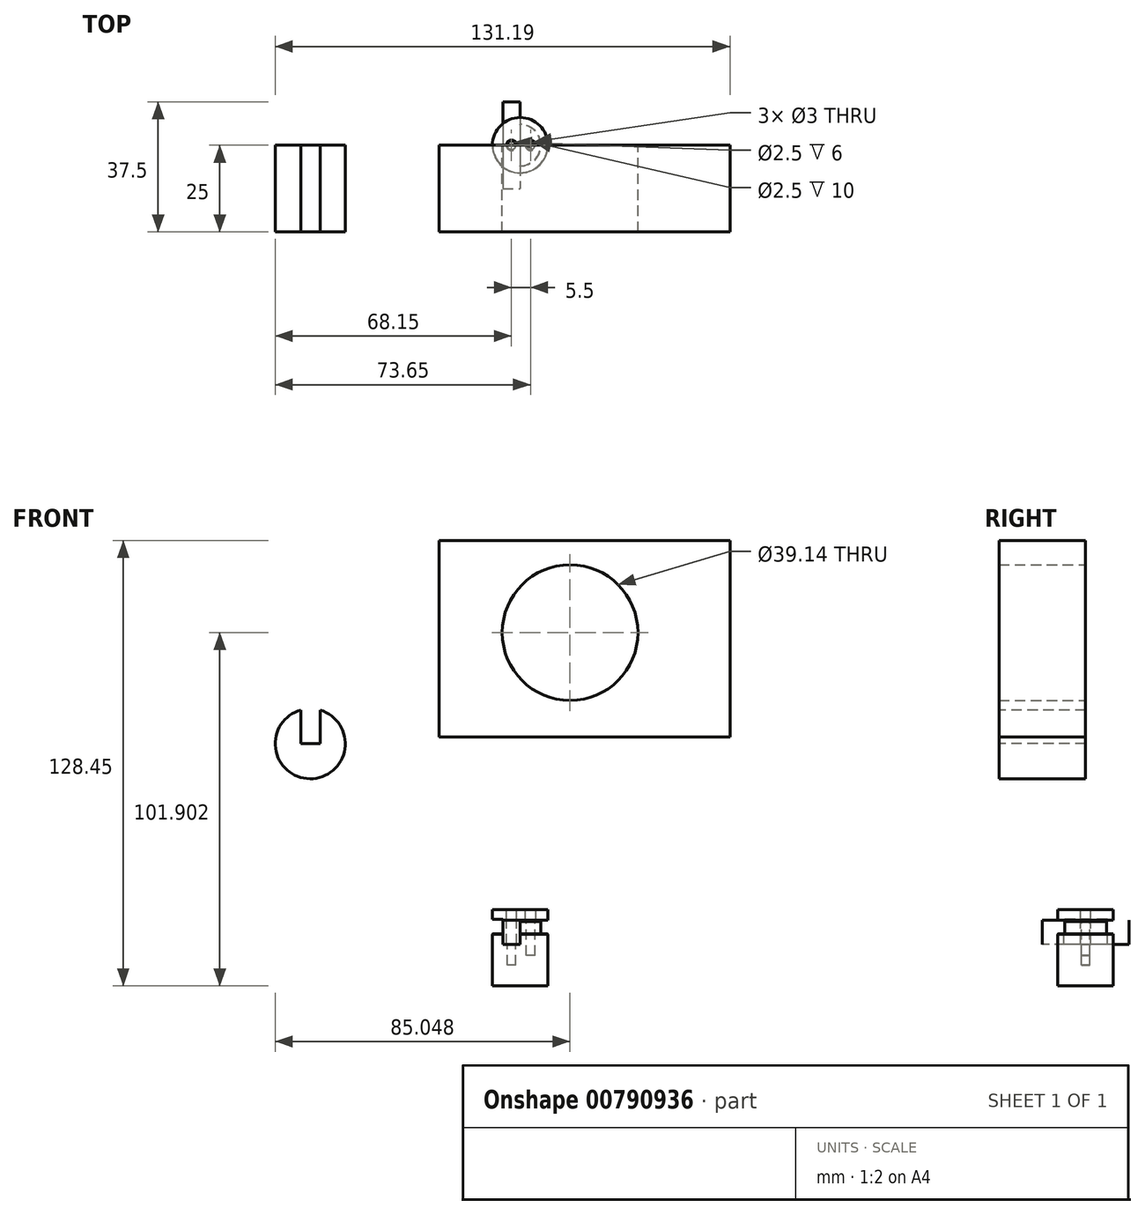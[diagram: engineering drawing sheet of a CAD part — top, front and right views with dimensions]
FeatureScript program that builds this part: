
annotation { "Feature Type Name" : "Feature", "Feature Type Description" : "" }
export const myFeature = defineFeature(function(context is Context, id is Id, definition is map)
    precondition{}
    {
        {
            var Q0;
            Q0=qCreatedBy(makeId("Top.planeOp"),FACE);
            var sketch = newSketch(context, id + "F0", { "sketchPlane" : qUnion([Q0])});
            skCircle(sketch, "E0", {"center": v(0, 0) * mm, "radius": 6 * mm});
            skSolve(sketch);
        }
        {
            var Q0;
            Q0 = qSketchRegion(id + "F0", true);
            extrude(context, id + "F1", {"entities" : qUnion([Q0]), "depth" : 3.75 * mm, "offsetDistance" : 25 * mm});
        }
        {
            var Q0;
            Q0=makeQuery(id+"F1.opExtrude","CAP_FACE",FACE,{"disambiguationData":[OSD([sQuery(id+"F0.wireOp",EDGE,"E0")])],"isStart":true});
            var sketch = newSketch(context, id + "F2", { "sketchPlane" : qUnion([Q0])});
            skCircle(sketch, "E1", {"center": v(0, 0) * mm, "radius": 8 * mm});
            skSolve(sketch);
        }
        {
            var Q0;
            Q0 = qSketchRegion(id + "F2", true);
            extrude(context, id + "F3", {"entities" : qUnion([Q0]), "operationType" : NewBodyOperationType.ADD, "depth" : 15 * mm, "offsetDistance" : 25 * mm});
        }
        {
            var Q0;
            Q0=makeQuery(id+"F1.opExtrude","CAP_EDGE",EDGE,{"disambiguationData":[OSD([sQuery(id+"F0.wireOp",EDGE,"E0")])],"isStart":false});
            var Q1;
            Q1=makeQuery(id+"F3.opExtrude","CAP_EDGE",EDGE,{"disambiguationData":[OSD([sQuery(id+"F2.wireOp",EDGE,"E1")])],"isStart":true});
            chamfer(context, id + "F4", {"entities" : qUnion([Q0, Q1]), "width" : .1 * mm, "tangentPropagation" : true});
        }
        {
            var Q0;
            Q0=makeQuery(id+"F1.opExtrude","CAP_FACE",FACE,{"disambiguationData":[OSD([sQuery(id+"F0.wireOp",EDGE,"E0")])],"isStart":false});
            var sketch = newSketch(context, id + "F5", { "sketchPlane" : qUnion([Q0])});
            skArc(sketch, "E2.0", {"start": v(0, 6) * mm, "mid": v(-6, 0) * mm, "end": v(0, -6) * mm});
            skLineSegment(sketch, "E3", {"start": v(0, 6) * mm, "end": v(0, -6) * mm});
            skSolve(sketch);
        }
        {
            var Q0;
            Q0 = qSketchRegion(id + "F5", true);
            var Q1;
            Q1=makeQuery(id+"F3.opExtrude","CAP_FACE",FACE,{"disambiguationData":[OSD([sQuery(id+"F2.wireOp",EDGE,"E1")])],"isStart":true});
            extrude(context, id + "F6", {"entities" : qUnion([Q0]), "operationType" : NewBodyOperationType.REMOVE, "endBound" : BoundingType.UP_TO_SURFACE, "oppositeDirection" : true, "depth" : .5 * mm, "endBoundEntityFace" : qUnion([Q1]), "offsetDistance" : 25 * mm});
        }
        {
            var Q0;
            Q0=makeQuery(id+"F6.boolean.opBoolean","MERGE",FACE,{"derivedFrom":[makeQuery(id+"F3.opExtrude","CAP_FACE",FACE,{"disambiguationData":[OSD([sQuery(id+"F2.wireOp",EDGE,"E1")])],"isStart":true})],"fromTools":[makeQuery(id+"F6.opExtrude","CAP_FACE",FACE,{"disambiguationData":[OSD([sQuery(id+"F5.wireOp",EDGE,"E2.0"),sQuery(id+"F5.wireOp",EDGE,"E3")])],"isStart":false})]});
            var sketch = newSketch(context, id + "F7", { "sketchPlane" : qUnion([Q0])});
            skLineSegment(sketch, "E4.bottom", {"start": v(-5, 12.5) * mm, "end": v(0, 12.5) * mm});
            skLineSegment(sketch, "E4.top", {"start": v(-5, -12.5) * mm, "end": v(0, -12.5) * mm});
            skLineSegment(sketch, "E4.left", {"start": v(-5, 12.5) * mm, "end": v(-5, -12.5) * mm});
            skLineSegment(sketch, "E4.right", {"start": v(0, 12.5) * mm, "end": v(0, -12.5) * mm});
            skSolve(sketch);
        }
        {
            var Q0;
            Q0 = qSketchRegion(id + "F7", true);
            extrude(context, id + "F8", {"entities" : qUnion([Q0]), "operationType" : NewBodyOperationType.REMOVE, "oppositeDirection" : true, "depth" : 3 * mm, "offsetDistance" : 25 * mm});
        }
        {
            var Q0;
            Q0=makeQuery(id+"F8.boolean.opBoolean","COPY",FACE,{"derivedFrom":makeQuery(id+"F8.opExtrude","CAP_FACE",FACE,{"disambiguationData":[OSD([sQuery(id+"F7.wireOp",EDGE,"E4.bottom"),sQuery(id+"F7.wireOp",EDGE,"E4.top"),sQuery(id+"F7.wireOp",EDGE,"E4.left"),sQuery(id+"F7.wireOp",EDGE,"E4.right")])],"isStart":false})});
            var sketch = newSketch(context, id + "F9", { "sketchPlane" : qUnion([Q0])});
            skLineSegment(sketch, "E5.0", {"start": v(-5, 12.5) * mm, "end": v(0, 12.5) * mm});
            skLineSegment(sketch, "E5.1", {"start": v(-5, -12.5) * mm, "end": v(0, -12.5) * mm});
            skLineSegment(sketch, "E5.2", {"start": v(-5, 12.5) * mm, "end": v(-5, -12.5) * mm});
            skLineSegment(sketch, "E5.3", {"start": v(0, 12.5) * mm, "end": v(0, -12.5) * mm});
            skSolve(sketch);
        }
        {
            var Q0;
            Q0 = qSketchRegion(id + "F9", true);
            extrude(context, id + "F10", {"entities" : qUnion([Q0]), "depth" : 7 * mm, "offsetDistance" : 25 * mm});
        }
        {
            var Q0;
            Q0=makeQuery(id+"F10.opExtrude","CAP_FACE",FACE,{"disambiguationData":[OSD([sQuery(id+"F9.wireOp",EDGE,"E5.0"),sQuery(id+"F9.wireOp",EDGE,"E5.1"),sQuery(id+"F9.wireOp",EDGE,"E5.2"),sQuery(id+"F9.wireOp",EDGE,"E5.3")])],"isStart":false});
            var sketch = newSketch(context, id + "F11", { "sketchPlane" : qUnion([Q0])});
            skCircle(sketch, "E6", {"center": v(0, 0) * mm, "radius": 8 * mm});
            skSolve(sketch);
        }
        {
            var Q0;
            Q0 = qSketchRegion(id + "F11", true);
            extrude(context, id + "F12", {"entities" : qUnion([Q0]), "depth" : 3 * mm, "offsetDistance" : 25 * mm});
        }
        {
            var Q0;
            Q0=makeQuery(id+"F12.opExtrude","CAP_FACE",FACE,{"disambiguationData":[OSD([sQuery(id+"F11.wireOp",EDGE,"E6")])],"isStart":false});
            var sketch = newSketch(context, id + "F13", { "sketchPlane" : qUnion([Q0])});
            skCircle(sketch, "E7", {"center": v(3, 0) * mm, "radius": 1.5 * mm});
            skSolve(sketch);
        }
        {
            var Q0;
            Q0 = qSketchRegion(id + "F13", true);
            var Q1;
            Q1=makeQuery(id+"F12.opExtrude","CAP_FACE",FACE,{"disambiguationData":[OSD([sQuery(id+"F11.wireOp",EDGE,"E6")])],"isStart":true});
            extrude(context, id + "F14", {"entities" : qUnion([Q0]), "operationType" : NewBodyOperationType.REMOVE, "endBound" : BoundingType.UP_TO_SURFACE, "oppositeDirection" : true, "depth" : 15 * mm, "endBoundEntityFace" : qUnion([Q1]), "offsetDistance" : 25 * mm});
        }
        {
            var Q0;
            Q0=makeQuery(id+"F12.opExtrude","CAP_FACE",FACE,{"disambiguationData":[OSD([sQuery(id+"F11.wireOp",EDGE,"E6")])],"isStart":false});
            var sketch = newSketch(context, id + "F15", { "sketchPlane" : qUnion([Q0])});
            skLineSegment(sketch, "E8", {"start": v(-2.5, 12.5) * mm, "end": v(-2.5, -12.5) * mm, "construction": true});
            skCircle(sketch, "E9", {"center": v(-2.5, 0) * mm, "radius": 1.5 * mm});
            skSolve(sketch);
        }
        {
            var Q0;
            Q0 = qSketchRegion(id + "F15", true);
            var Q1;
            Q1=makeQuery(id+"F10.opExtrude","CAP_FACE",FACE,{"disambiguationData":[OSD([sQuery(id+"F9.wireOp",EDGE,"E5.0"),sQuery(id+"F9.wireOp",EDGE,"E5.1"),sQuery(id+"F9.wireOp",EDGE,"E5.2"),sQuery(id+"F9.wireOp",EDGE,"E5.3")])],"isStart":true});
            extrude(context, id + "F16", {"entities" : qUnion([Q0]), "operationType" : NewBodyOperationType.REMOVE, "endBound" : BoundingType.UP_TO_SURFACE, "oppositeDirection" : true, "depth" : 15 * mm, "endBoundEntityFace" : qUnion([Q1]), "offsetDistance" : 25 * mm});
        }
        {
            var Q0;
            Q0=makeQuery(id+"F8.boolean.opBoolean","COPY",FACE,{"derivedFrom":makeQuery(id+"F8.opExtrude","CAP_FACE",FACE,{"disambiguationData":[OSD([sQuery(id+"F7.wireOp",EDGE,"E4.bottom"),sQuery(id+"F7.wireOp",EDGE,"E4.top"),sQuery(id+"F7.wireOp",EDGE,"E4.left"),sQuery(id+"F7.wireOp",EDGE,"E4.right")])],"isStart":false})});
            var sketch = newSketch(context, id + "F17", { "sketchPlane" : qUnion([Q0])});
            skCircle(sketch, "E10", {"center": v(-2.5, 0) * mm, "radius": 1.25 * mm});
            skSolve(sketch);
        }
        {
            var Q0;
            Q0 = qSketchRegion(id + "F17", true);
            extrude(context, id + "F18", {"entities" : qUnion([Q0]), "operationType" : NewBodyOperationType.REMOVE, "oppositeDirection" : true, "depth" : 6 * mm, "offsetDistance" : 25 * mm});
        }
        {
            var Q0;
            Q0=makeQuery(id+"F1.opExtrude","CAP_FACE",FACE,{"disambiguationData":[OSD([sQuery(id+"F0.wireOp",EDGE,"E0")])],"isStart":false});
            var sketch = newSketch(context, id + "F19", { "sketchPlane" : qUnion([Q0])});
            skCircle(sketch, "E11", {"center": v(3, 0) * mm, "radius": 1.25 * mm});
            skPoint(sketch, "E11.centerSnap0", {"position": v(5.9, 0) * mm});
            skSolve(sketch);
        }
        {
            var Q0;
            Q0 = qSketchRegion(id + "F19", true);
            extrude(context, id + "F20", {"entities" : qUnion([Q0]), "operationType" : NewBodyOperationType.REMOVE, "oppositeDirection" : true, "depth" : 10 * mm, "offsetDistance" : 25 * mm});
        }
        {
            var Q0;
            Q0=makeQuery(id+"F12.opExtrude","CAP_FACE",FACE,{"disambiguationData":[OSD([sQuery(id+"F11.wireOp",EDGE,"E6")])],"isStart":true});
            var sketch = newSketch(context, id + "F21", { "sketchPlane" : qUnion([Q0])});
            skArc(sketch, "E12.0", {"start": v(-5, -6.24) * mm, "mid": v(-3.58, -7.15) * mm, "end": v(-2, -7.75) * mm});
            skLineSegment(sketch, "E13.0", {"start": v(-5, -6.24) * mm, "end": v(-5, 6.24) * mm});
            skLineSegment(sketch, "E14", {"start": v(-2, -7.75) * mm, "end": v(-2, 7.75) * mm});
            skPoint(sketch, "E15.orphan", {"position": v(-5, -12.5) * mm});
            skPoint(sketch, "E16.orphan", {"position": v(-5, 12.5) * mm});
            skArc(sketch, "E17.trimOffspring", {"start": v(-2, 7.75) * mm, "mid": v(-3.58, 7.15) * mm, "end": v(-5, 6.24) * mm});
            skSolve(sketch);
        }
        {
            var Q0;
            Q0=makeQuery(id+"F21.imprint","IMPRINT",FACE,{"disambiguationData":[TD([[makeQuery(id+"F21.imprint","IMPRINT",EDGE,{"derivedFrom":makeQuery(id+"F14.boolean.opBoolean","COPY",EDGE,{"derivedFrom":makeQuery(id+"F14.opExtrude","CAP_EDGE",EDGE,{"disambiguationData":[OSD([sQuery(id+"F13.wireOp",EDGE,"E7")])],"isStart":false})})}),-1.0]])]});
            var Q1;
            {var subQ0=sQuery(id+"F21.wireOp",EDGE,"E13.0");Q1=makeQuery(id+"F21.imprint","IMPRINT",FACE,{"disambiguationData":[TD([[makeQuery(id+"F21.imprint","IMPRINT",EDGE,{"derivedFrom":subQ0}),1.0]])]});}
            extrude(context, id + "F22", {"entities" : qUnion([Q0, Q1]), "operationType" : NewBodyOperationType.REMOVE, "oppositeDirection" : true, "depth" : .25 * mm, "offsetDistance" : 25 * mm});
        }
        {
            var Q0;
            Q0=qCreatedBy(makeId("Front.planeOp"),FACE);
            var sketch = newSketch(context, id + "F23", { "sketchPlane" : qUnion([Q0])});
            skCircle(sketch, "E18", {"center": v(-60.54, 54.86) * mm, "radius": 10.1 * mm});
            skSolve(sketch);
        }
        {
            var Q0;
            Q0 = qSketchRegion(id + "F23", true);
            extrude(context, id + "F24", {"entities" : qUnion([Q0]), "depth" : 25 * mm, "offsetDistance" : 25 * mm});
        }
        {
            var Q0;
            Q0=qCreatedBy(makeId("Front.planeOp"),FACE);
            var sketch = newSketch(context, id + "F25", { "sketchPlane" : qUnion([Q0])});
            skLineSegment(sketch, "E19.bottom", {"start": v(-23.42, 113.45) * mm, "end": v(60.54, 113.45) * mm});
            skLineSegment(sketch, "E19.top", {"start": v(-23.42, 56.85) * mm, "end": v(60.54, 56.85) * mm});
            skLineSegment(sketch, "E19.left", {"start": v(-23.42, 113.45) * mm, "end": v(-23.42, 56.85) * mm});
            skLineSegment(sketch, "E19.right", {"start": v(60.54, 113.45) * mm, "end": v(60.54, 56.85) * mm});
            skCircle(sketch, "E20", {"center": v(14.4, 86.9) * mm, "radius": 19.57 * mm});
            skSolve(sketch);
        }
        {
            var Q0;
            Q0 = qSketchRegion(id + "F25", true);
            extrude(context, id + "F26", {"entities" : qUnion([Q0]), "depth" : 25 * mm, "offsetDistance" : 25 * mm});
        }
        {
            var Q0;
            Q0=makeQuery(id+"F24.opExtrude","CAP_FACE",FACE,{"disambiguationData":[OSD([sQuery(id+"F23.wireOp",EDGE,"E18")])],"isStart":false});
            var sketch = newSketch(context, id + "F27", { "sketchPlane" : qUnion([Q0])});
            skArc(sketch, "E21.0", {"start": v(-57.64, 64.54) * mm, "mid": v(-60.44, 64.96) * mm, "end": v(-63.24, 64.6) * mm});
            skLineSegment(sketch, "E22", {"start": v(-63.24, 64.6) * mm, "end": v(-63.24, 54.92) * mm});
            skLineSegment(sketch, "E23", {"start": v(-63.24, 54.92) * mm, "end": v(-57.64, 54.86) * mm});
            skLineSegment(sketch, "E24", {"start": v(-57.64, 54.86) * mm, "end": v(-57.64, 64.54) * mm});
            skSolve(sketch);
        }
        {
            var Q0;
            Q0 = qSketchRegion(id + "F27", true);
            extrude(context, id + "F28", {"entities" : qUnion([Q0]), "operationType" : NewBodyOperationType.REMOVE, "oppositeDirection" : true, "depth" : 25 * mm, "offsetDistance" : 25 * mm});
        }
    });
